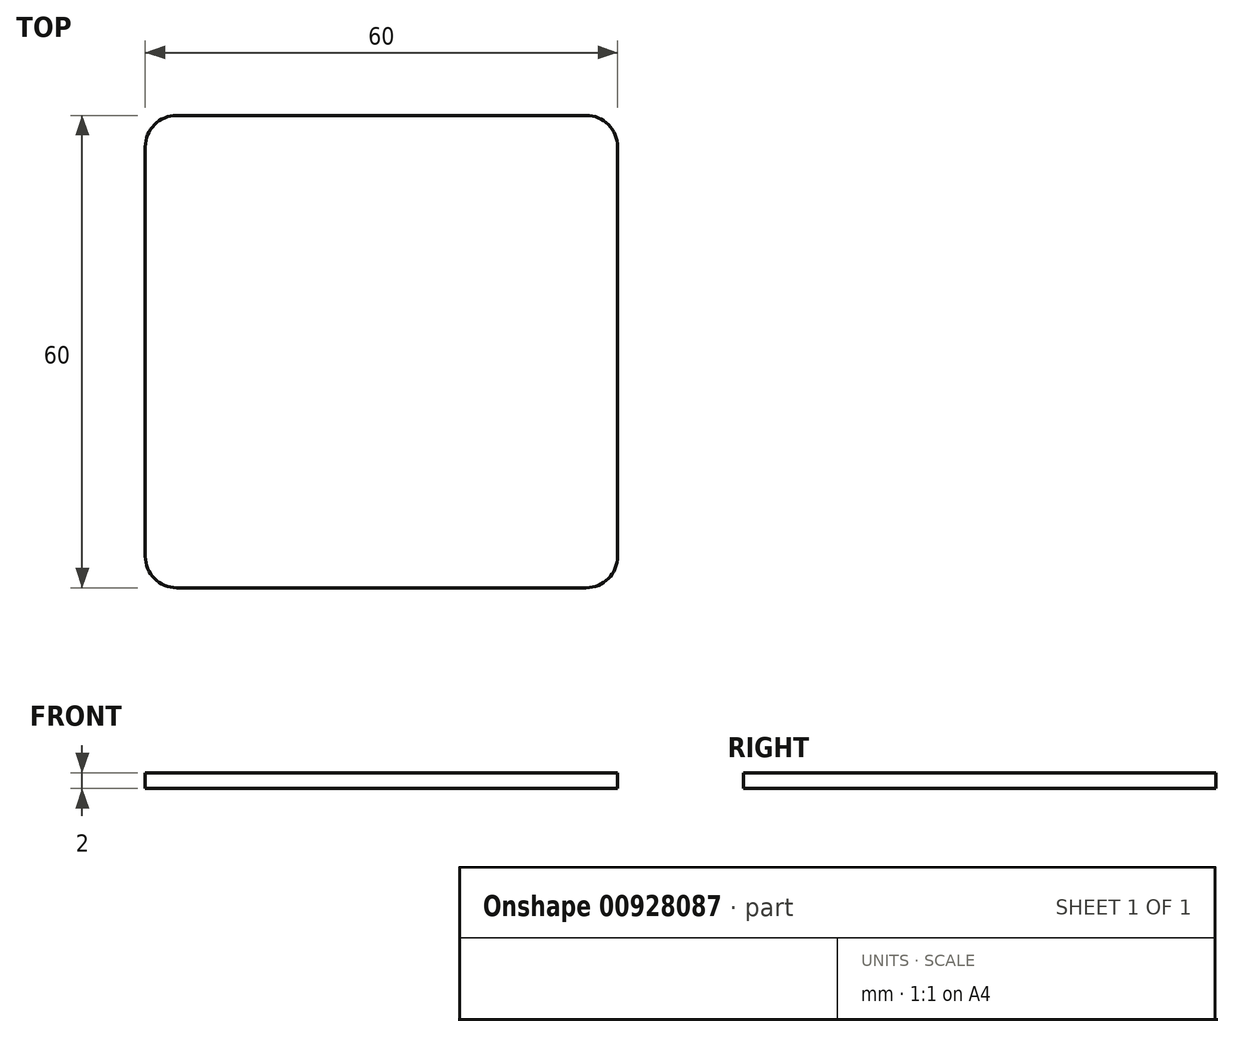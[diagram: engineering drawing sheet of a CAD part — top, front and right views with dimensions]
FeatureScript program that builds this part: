
annotation { "Feature Type Name" : "Feature", "Feature Type Description" : "" }
export const myFeature = defineFeature(function(context is Context, id is Id, definition is map)
    precondition{}
    {
        {
            var Q0;
            Q0=qCreatedBy(makeId("Top.planeOp"),FACE);
            var sketch = newSketch(context, id + "F0", { "sketchPlane" : qUnion([Q0])});
            skLineSegment(sketch, "E0.bottom", {"start": v(-26, 30) * mm, "end": v(26, 30) * mm});
            skLineSegment(sketch, "E0.top", {"start": v(-26, -30) * mm, "end": v(26, -30) * mm});
            skLineSegment(sketch, "E0.left", {"start": v(-30, 26) * mm, "end": v(-30, -26) * mm});
            skLineSegment(sketch, "E0.right", {"start": v(30, 26) * mm, "end": v(30, -26) * mm});
            skPoint(sketch, "E0.middle", {"position": v(0, 0) * mm});
            skPoint(sketch, "E1.visualSharp", {"position": v(-30, 30) * mm});
            skArc(sketch, "E1.filletArc", {"start": v(-26, 30) * mm, "mid": v(-28.83, 28.83) * mm, "end": v(-30, 26) * mm});
            skPoint(sketch, "E2.visualSharp", {"position": v(30, 30) * mm});
            skArc(sketch, "E2.filletArc", {"start": v(30, 26) * mm, "mid": v(28.83, 28.83) * mm, "end": v(26, 30) * mm});
            skPoint(sketch, "E3.visualSharp", {"position": v(30, -30) * mm});
            skArc(sketch, "E3.filletArc", {"start": v(26, -30) * mm, "mid": v(28.83, -28.83) * mm, "end": v(30, -26) * mm});
            skPoint(sketch, "E4.visualSharp", {"position": v(-30, -30) * mm});
            skArc(sketch, "E4.filletArc", {"start": v(-30, -26) * mm, "mid": v(-28.83, -28.83) * mm, "end": v(-26, -30) * mm});
            skSolve(sketch);
        }
        {
            var Q0;
            Q0=makeQuery(id+"F0.imprint","IMPRINT",FACE,{"disambiguationData":[TD([[makeQuery(id+"F0.imprint","IMPRINT",EDGE,{"derivedFrom":sQuery(id+"F0.wireOp",EDGE,"E0.bottom")}),-1.0]])]});
            extrude(context, id + "F1", {"entities" : qUnion([Q0]), "depth" : 2 * mm, "offsetDistance" : 25 * mm});
        }
    });
